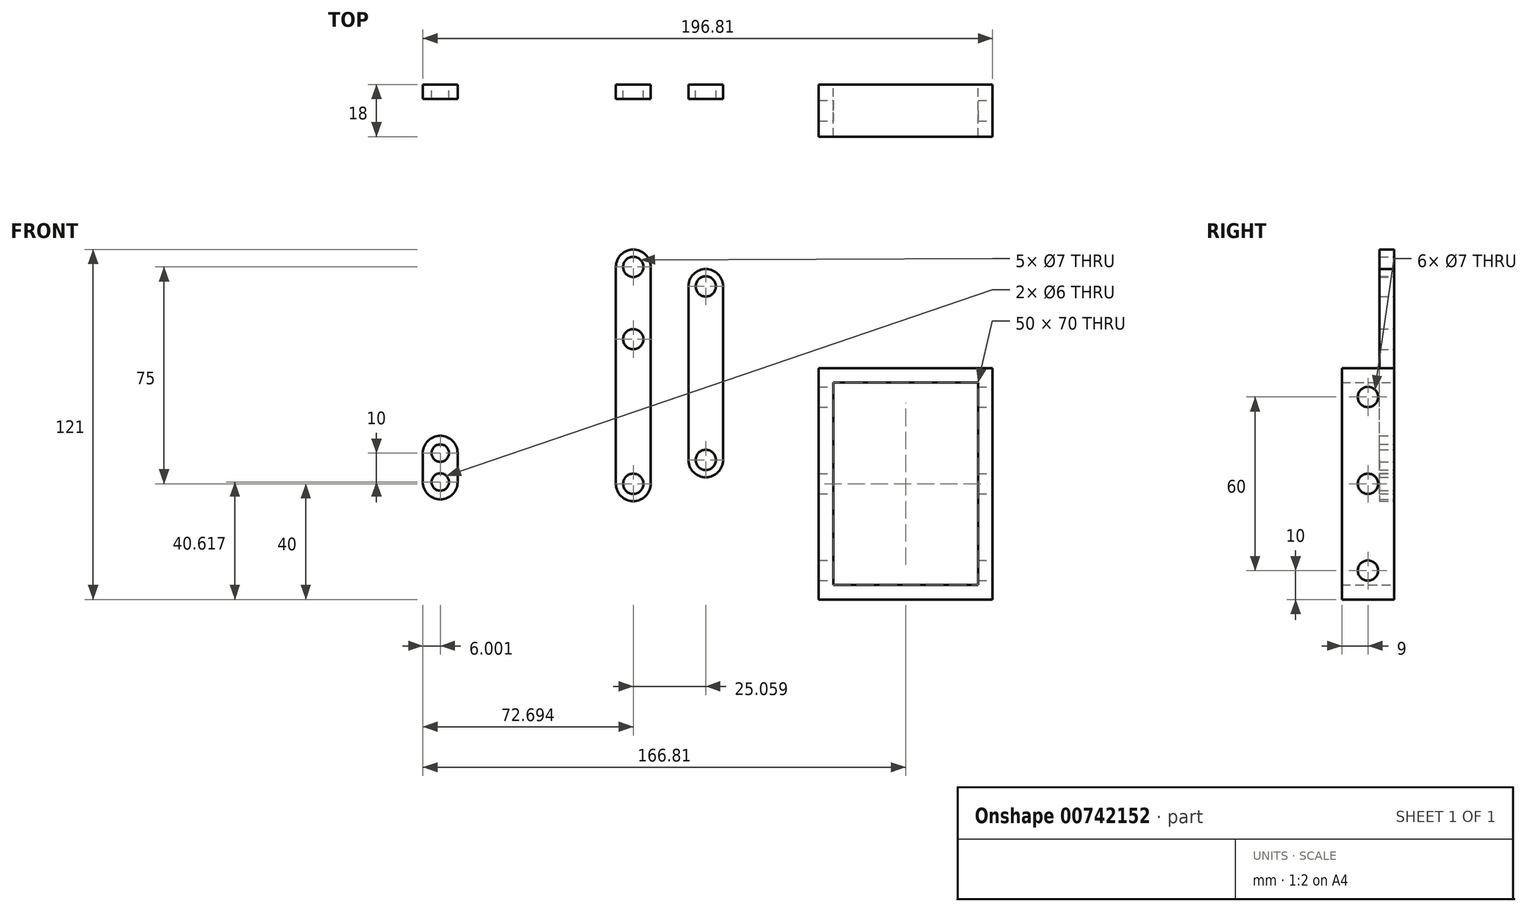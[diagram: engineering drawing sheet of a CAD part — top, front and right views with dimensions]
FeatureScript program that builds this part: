
annotation { "Feature Type Name" : "Feature", "Feature Type Description" : "" }
export const myFeature = defineFeature(function(context is Context, id is Id, definition is map)
    precondition{}
    {
        {
            var Q0;
            Q0=qCreatedBy(makeId("Front.planeOp"),FACE);
            var sketch = newSketch(context, id + "F0", { "sketchPlane" : qUnion([Q0])});
            skLineSegment(sketch, "E0.bottom", {"start": v(-25, -35) * mm, "end": v(25, -35) * mm});
            skLineSegment(sketch, "E0.top", {"start": v(-25, 35) * mm, "end": v(25, 35) * mm});
            skLineSegment(sketch, "E0.left", {"start": v(-25, -35) * mm, "end": v(-25, 35) * mm});
            skLineSegment(sketch, "E0.right", {"start": v(25, -35) * mm, "end": v(25, 35) * mm});
            skPoint(sketch, "E0.middle", {"position": v(0, 0) * mm});
            skLineSegment(sketch, "E1.bottom", {"start": v(-30, -40) * mm, "end": v(30, -40) * mm});
            skLineSegment(sketch, "E1.top", {"start": v(-30, 40) * mm, "end": v(30, 40) * mm});
            skLineSegment(sketch, "E1.left", {"start": v(-30, -40) * mm, "end": v(-30, 40) * mm});
            skLineSegment(sketch, "E1.right", {"start": v(30, -40) * mm, "end": v(30, 40) * mm});
            skSolve(sketch);
        }
        {
            var Q0;
            Q0 = qSketchRegion(id + "F0", true);
            extrude(context, id + "F1", {"entities" : qUnion([Q0]), "depth" : 18 * mm, "offsetDistance" : 25 * mm});
        }
        {
            var Q0;
            Q0=makeQuery(id+"F1.opExtrude","SWEPT_FACE",FACE,{"disambiguationData":[OSD([sQuery(id+"F0.wireOp",EDGE,"E1.right")])]});
            var sketch = newSketch(context, id + "F2", { "sketchPlane" : qUnion([Q0])});
            skCircle(sketch, "E2", {"center": v(-9, -30) * mm, "radius": 3.5 * mm});
            skCircle(sketch, "E3", {"center": v(-9, 0) * mm, "radius": 3.5 * mm});
            skCircle(sketch, "E4", {"center": v(-9, 30) * mm, "radius": 3.5 * mm});
            skSolve(sketch);
        }
        {
            var Q0;
            Q0 = qSketchRegion(id + "F2", true);
            extrude(context, id + "F3", {"entities" : qUnion([Q0]), "operationType" : NewBodyOperationType.REMOVE, "endBound" : BoundingType.THROUGH_ALL, "oppositeDirection" : true, "depth" : 25 * mm, "offsetDistance" : 25 * mm});
        }
        {
            var Q0;
            Q0=qCreatedBy(makeId("Front.planeOp"),FACE);
            var sketch = newSketch(context, id + "F4", { "sketchPlane" : qUnion([Q0])});
            skLineSegment(sketch, "E5.left", {"start": v(-88.12, 0) * mm, "end": v(-88.12, 75) * mm});
            skLineSegment(sketch, "E5.right", {"start": v(-100.12, 0) * mm, "end": v(-100.12, 75) * mm});
            skPoint(sketch, "E5.middle", {"position": v(-94.12, 37.5) * mm});
            skArc(sketch, "E6", {"start": v(-88.12, 75) * mm, "mid": v(-94.12, 81) * mm, "end": v(-100.12, 75) * mm});
            skArc(sketch, "E7", {"start": v(-100.12, 0) * mm, "mid": v(-94.12, -6) * mm, "end": v(-88.12, 0) * mm});
            skCircle(sketch, "E8", {"center": v(-94.12, 75) * mm, "radius": 3.5 * mm});
            skCircle(sketch, "E9", {"center": v(-94.12, 0) * mm, "radius": 3.5 * mm});
            skCircle(sketch, "E10", {"center": v(-94.12, 50) * mm, "radius": 3.5 * mm});
            skSolve(sketch);
        }
        {
            var Q0;
            Q0 = qSketchRegion(id + "F4", true);
            extrude(context, id + "F5", {"entities" : qUnion([Q0]), "depth" : 5 * mm, "offsetDistance" : 25 * mm});
        }
        {
            var Q0;
            Q0=qCreatedBy(makeId("Front.planeOp"),FACE);
            var sketch = newSketch(context, id + "F6", { "sketchPlane" : qUnion([Q0])});
            skLineSegment(sketch, "E11.left", {"start": v(-63.06, 8.25) * mm, "end": v(-63.06, 68.25) * mm});
            skLineSegment(sketch, "E11.right", {"start": v(-75.06, 8.25) * mm, "end": v(-75.06, 68.25) * mm});
            skPoint(sketch, "E11.middle", {"position": v(-69.06, 38.25) * mm});
            skArc(sketch, "E12", {"start": v(-63.06, 68.25) * mm, "mid": v(-69.06, 74.25) * mm, "end": v(-75.06, 68.25) * mm});
            skArc(sketch, "E13", {"start": v(-75.06, 8.25) * mm, "mid": v(-69.06, 2.25) * mm, "end": v(-63.06, 8.25) * mm});
            skCircle(sketch, "E14", {"center": v(-69.06, 68.25) * mm, "radius": 3.5 * mm});
            skCircle(sketch, "E15", {"center": v(-69.06, 8.25) * mm, "radius": 3.5 * mm});
            skSolve(sketch);
        }
        {
            var Q0;
            Q0 = qSketchRegion(id + "F6", true);
            extrude(context, id + "F7", {"entities" : qUnion([Q0]), "depth" : 5 * mm, "offsetDistance" : 25 * mm});
        }
        {
            var Q0;
            Q0=qCreatedBy(makeId("Front.planeOp"),FACE);
            var sketch = newSketch(context, id + "F8", { "sketchPlane" : qUnion([Q0])});
            skLineSegment(sketch, "E16.left", {"start": v(-166.8, 0.62) * mm, "end": v(-166.8, 10.62) * mm});
            skLineSegment(sketch, "E16.right", {"start": v(-154.8, 0.62) * mm, "end": v(-154.8, 10.62) * mm});
            skPoint(sketch, "E16.middle", {"position": v(-160.8, 5.62) * mm});
            skArc(sketch, "E17", {"start": v(-154.8, 10.62) * mm, "mid": v(-160.8, 16.62) * mm, "end": v(-166.8, 10.62) * mm});
            skArc(sketch, "E18", {"start": v(-166.8, 0.62) * mm, "mid": v(-160.8, -5.38) * mm, "end": v(-154.8, 0.62) * mm});
            skCircle(sketch, "E19", {"center": v(-160.8, 0.62) * mm, "radius": 3 * mm});
            skCircle(sketch, "E20", {"center": v(-160.8, 10.62) * mm, "radius": 3 * mm});
            skSolve(sketch);
        }
        {
            var Q0;
            Q0 = qSketchRegion(id + "F8", true);
            extrude(context, id + "F9", {"entities" : qUnion([Q0]), "depth" : 5 * mm, "offsetDistance" : 25 * mm});
        }
    });
